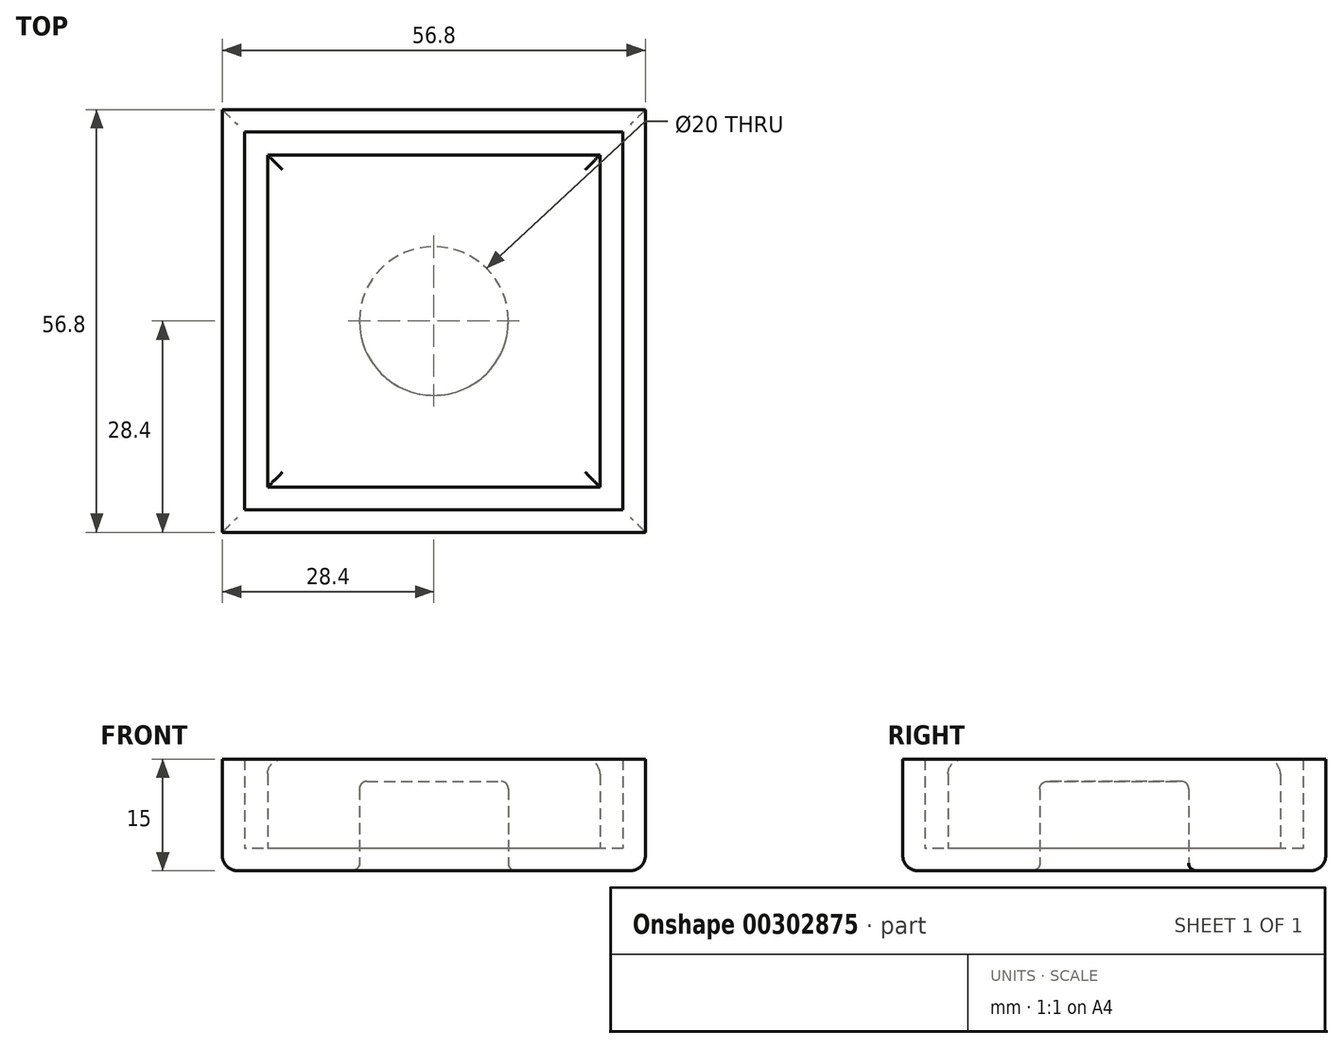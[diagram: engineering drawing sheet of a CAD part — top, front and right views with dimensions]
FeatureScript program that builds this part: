
annotation { "Feature Type Name" : "Feature", "Feature Type Description" : "" }
export const myFeature = defineFeature(function(context is Context, id is Id, definition is map)
    precondition{}
    {
        {
            var Q0;
            Q0=qCreatedBy(makeId("Top.planeOp"),FACE);
            var sketch = newSketch(context, id + "F0", { "sketchPlane" : qUnion([Q0])});
            skLineSegment(sketch, "E0.bottom", {"start": v(25.4, 25.4) * mm, "end": v(-25.4, 25.4) * mm});
            skLineSegment(sketch, "E0.top", {"start": v(25.4, -25.4) * mm, "end": v(-25.4, -25.4) * mm});
            skLineSegment(sketch, "E0.left", {"start": v(25.4, 25.4) * mm, "end": v(25.4, -25.4) * mm});
            skLineSegment(sketch, "E0.right", {"start": v(-25.4, 25.4) * mm, "end": v(-25.4, -25.4) * mm});
            skPoint(sketch, "E0.middle", {"position": v(0, 0) * mm});
            skLineSegment(sketch, "E1.bottom", {"start": v(28.4, 28.4) * mm, "end": v(-28.4, 28.4) * mm});
            skLineSegment(sketch, "E1.top", {"start": v(28.4, -28.4) * mm, "end": v(-28.4, -28.4) * mm});
            skLineSegment(sketch, "E1.left", {"start": v(28.4, 28.4) * mm, "end": v(28.4, -28.4) * mm});
            skLineSegment(sketch, "E1.right", {"start": v(-28.4, 28.4) * mm, "end": v(-28.4, -28.4) * mm});
            skLineSegment(sketch, "E2.bottom", {"start": v(22.33, 22.33) * mm, "end": v(-22.33, 22.33) * mm});
            skLineSegment(sketch, "E2.top", {"start": v(22.33, -22.32) * mm, "end": v(-22.33, -22.32) * mm});
            skLineSegment(sketch, "E2.left", {"start": v(22.33, 22.33) * mm, "end": v(22.33, -22.32) * mm});
            skLineSegment(sketch, "E2.right", {"start": v(-22.33, 22.33) * mm, "end": v(-22.33, -22.32) * mm});
            skSolve(sketch);
        }
        {
            var Q0;
            Q0=makeQuery(id+"F0.imprint","IMPRINT",FACE,{"disambiguationData":[TD([[makeQuery(id+"F0.imprint","IMPRINT",EDGE,{"derivedFrom":sQuery(id+"F0.wireOp",EDGE,"E0.bottom")}),1.0]])]});
            extrude(context, id + "F1", {"entities" : qUnion([Q0]), "depth" : 3 * mm});
        }
        {
            var Q0;
            Q0=makeQuery(id+"F0.imprint","IMPRINT",FACE,{"disambiguationData":[TD([[makeQuery(id+"F0.imprint","IMPRINT",EDGE,{"derivedFrom":sQuery(id+"F0.wireOp",EDGE,"E0.bottom")}),-1.0]])]});
            var Q1;
            Q1=makeQuery(id+"F0.imprint","IMPRINT",FACE,{"disambiguationData":[TD([[makeQuery(id+"F0.imprint","IMPRINT",EDGE,{"derivedFrom":sQuery(id+"F0.wireOp",EDGE,"E2.bottom")}),1.0]])]});
            extrude(context, id + "F2", {"entities" : qUnion([Q0, Q1]), "operationType" : NewBodyOperationType.ADD, "depth" : 15 * mm});
        }
        {
            var Q0;
            Q0=makeQuery(id+"F2.opExtrude","CAP_FACE",FACE,{"disambiguationData":[OSD([sQuery(id+"F0.wireOp",EDGE,"E2.bottom"),sQuery(id+"F0.wireOp",EDGE,"E2.top"),sQuery(id+"F0.wireOp",EDGE,"E2.left"),sQuery(id+"F0.wireOp",EDGE,"E2.right")])],"isStart":false});
            fillet(context, id + "F3", {"entities" : qUnion([Q0]), "radius" : 2 * mm, "tangentPropagation" : true, "allowEdgeOverflow" : false});
        }
        {
            var Q0;
            {var subQ0=sQuery(id+"F0.wireOp",EDGE,"E2.right");var subQ1=sQuery(id+"F0.wireOp",EDGE,"E2.left");var subQ2=sQuery(id+"F0.wireOp",EDGE,"E2.top");var subQ3=sQuery(id+"F0.wireOp",EDGE,"E2.bottom");var subQ4=sQuery(id+"F0.wireOp",EDGE,"E0.right");var subQ5=sQuery(id+"F0.wireOp",EDGE,"E0.left");var subQ6=sQuery(id+"F0.wireOp",EDGE,"E0.top");var subQ7=sQuery(id+"F0.wireOp",EDGE,"E0.bottom");Q0=makeQuery(id+"F2.boolean.opBoolean","MERGE",FACE,{"derivedFrom":[makeQuery(id+"F1.opExtrude","CAP_FACE",FACE,{"disambiguationData":[OSD([subQ7,subQ6,subQ5,subQ4,subQ3,subQ2,subQ1,subQ0])],"isStart":true}),makeQuery(id+"F2.opExtrude","CAP_FACE",FACE,{"disambiguationData":[OSD([subQ7,subQ6,subQ5,subQ4,sQuery(id+"F0.wireOp",EDGE,"E1.bottom"),sQuery(id+"F0.wireOp",EDGE,"E1.top"),sQuery(id+"F0.wireOp",EDGE,"E1.left"),sQuery(id+"F0.wireOp",EDGE,"E1.right")])],"isStart":true}),makeQuery(id+"F2.opExtrude","CAP_FACE",FACE,{"disambiguationData":[OSD([subQ3,subQ2,subQ1,subQ0])],"isStart":true})]});}
            fillet(context, id + "F4", {"entities" : qUnion([Q0]), "radius" : 2 * mm, "tangentPropagation" : true, "allowEdgeOverflow" : false});
        }
        {
            var Q0;
            {var subQ0=sQuery(id+"F0.wireOp",EDGE,"E2.right");var subQ1=sQuery(id+"F0.wireOp",EDGE,"E2.left");var subQ2=sQuery(id+"F0.wireOp",EDGE,"E2.top");var subQ3=sQuery(id+"F0.wireOp",EDGE,"E2.bottom");var subQ4=sQuery(id+"F0.wireOp",EDGE,"E0.right");var subQ5=sQuery(id+"F0.wireOp",EDGE,"E0.left");var subQ6=sQuery(id+"F0.wireOp",EDGE,"E0.top");var subQ7=sQuery(id+"F0.wireOp",EDGE,"E0.bottom");Q0=makeQuery(id+"F2.boolean.opBoolean","MERGE",FACE,{"derivedFrom":[makeQuery(id+"F1.opExtrude","CAP_FACE",FACE,{"disambiguationData":[OSD([subQ7,subQ6,subQ5,subQ4,subQ3,subQ2,subQ1,subQ0])],"isStart":true}),makeQuery(id+"F2.opExtrude","CAP_FACE",FACE,{"disambiguationData":[OSD([subQ7,subQ6,subQ5,subQ4,sQuery(id+"F0.wireOp",EDGE,"E1.bottom"),sQuery(id+"F0.wireOp",EDGE,"E1.top"),sQuery(id+"F0.wireOp",EDGE,"E1.left"),sQuery(id+"F0.wireOp",EDGE,"E1.right")])],"isStart":true}),makeQuery(id+"F2.opExtrude","CAP_FACE",FACE,{"disambiguationData":[OSD([subQ3,subQ2,subQ1,subQ0])],"isStart":true})]});}
            var sketch = newSketch(context, id + "F5", { "sketchPlane" : qUnion([Q0])});
            skCircle(sketch, "E3", {"center": v(0, 0) * mm, "radius": 10 * mm});
            skSolve(sketch);
        }
        {
            var Q0;
            Q0=makeQuery(id+"F5.imprint","IMPRINT",FACE,{"disambiguationData":[TD([[makeQuery(id+"F5.imprint","IMPRINT",EDGE,{"derivedFrom":sQuery(id+"F5.wireOp",EDGE,"E3")}),1.0]])]});
            extrude(context, id + "F6", {"entities" : qUnion([Q0]), "operationType" : NewBodyOperationType.REMOVE, "oppositeDirection" : true, "depth" : 12 * mm});
        }
        {
            var Q0;
            Q0=makeQuery(id+"F6.boolean.opBoolean","COPY",FACE,{"derivedFrom":makeQuery(id+"F6.opExtrude","SWEPT_FACE",FACE,{"disambiguationData":[OSD([sQuery(id+"F5.wireOp",EDGE,"E3")])]})});
            fillet(context, id + "F7", {"entities" : qUnion([Q0]), "radius" : 1 * mm, "tangentPropagation" : true, "allowEdgeOverflow" : false});
        }
    });
